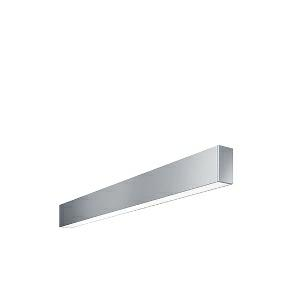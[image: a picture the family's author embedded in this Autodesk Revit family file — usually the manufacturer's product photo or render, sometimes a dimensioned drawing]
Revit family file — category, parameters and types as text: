
# Revit family: idoo_line_-_ilw_3000_840_d_00808325_902e
name_source: partatom
category: Lighting Fixtures
units: mm (PartAtom-declared; Revit-internal decimal feet)

## family parameters
Cut with Voids When Loaded = No
Host = Face
Light Source = No
Part Type = Normal
Room Calculation Point = No
Round Connector Dimension = Use Diameter
Shared = No

## types (1)
- IDOO.line - ILW 3000/840/D (1 x LED, 3150 lm, 4000K)
    Apparent Load = 23 VA
    Approval mark = CE
    CIE Flux Codes = 66 91 98 40 100
    Color Rendering = 80-89
    Color Temperature = 4000K
    Control Gear = Electronic ballast
    Default Elevation = 2000 mm  [stored 6.56168 ft]
    Description = ILW 3000/840/D|Wall-mounted luminaire|light source:  |work equipment: Adjustable electronic ballast, digital DALI|connected load: 220-240V, 50/60Hz|Power consumption: approx. 23 W|standby: approx. 0,25|power factor: approx. 0,970|luminous flux: 3150 lm|luminous efficacy: 136 lm/W|light distribution: Direct/indirect|direct ratio: approx. 40 %|colour temperature: Cold white, ca. 4000 K|color rendering index (CRI): >= 80|chromaticity tolerance:  3 SDCM|technology: Continuously dimmable|operation: External|luminaire body|material: Sectional aluminium|colour: Silver|lamp cover: Acrylic (PMMA), Clear|weight (net): approx. 4.7 kg|mains lead: Connector|design: Mounted version|Fastening: Mounting rail|glare control: Prism aperture|luminance(L65): <= 2700 cd/m|unified glare rating(4H 8H): <=  16|special features: DALI Load 1x, TouchDIM - dimming via standard switch, Flicker-free, Suitable as emergency lighting|
    Frequency = 50 Hz
    Height = 110 mm
    Lamp = 1 x LED
    Lamp Light Flux = 3150 lm
    Lamp count = 1
    Length = 1134 mm
    Luminous efficacy = 137 lm/W
    Manufacturer = Waldmann
    ModVariant = No
    Model = 00808325
    Mounting Place = Wall
    Mounting Type = Surface mounted
    Number of Poles = 1
    OnlyDefault = Yes
    Power Factor = 1
    Product Name = IDOO.line - ILW 3000/840/D
    Product group = Wall mounted Luminaire
    ProductGroupID = 20
    Protection Class = Protection class I
    Protection Degree = IP 40
    RLX_Detail_Level = 1
    RLX_Emergency_Light_Flux = 0 lm
    RLX_Emergency_Type = 0
    RLX_Emergency_Type_DB = No
    RlxData = <blob elided: 34593 chars, md5=d5333229>
    Socket = socket
    Standby Power = 0 W
    System Light Flux = 3150 lm
    System Power = 23 W
    Type Comments = Product without accessories
    Type Image = 113975000-00757981.jpg
    URL = http://relux.com
    VarID = ---
    Voltage = 230 V
    Voltage Range = 220-240 V
    Weight = 0.00 kg
    Width = 60 mm  [stored 0.19685 ft]

note: [stored X ft] marks values corroborated as IEEE doubles in the binary element streams (Revit-internal decimal feet)

## geometry (parser evidence)
native form markers: Blend x4, Sweep x14
no freeform markers — native parametric forms only
